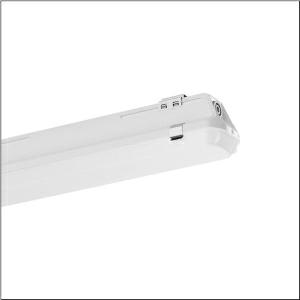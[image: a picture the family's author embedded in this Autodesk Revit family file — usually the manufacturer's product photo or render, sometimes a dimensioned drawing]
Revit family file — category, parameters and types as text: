
# Revit family: monsun_r__11_51fp208p430h_cbd4
name_source: partatom
category: Lighting Fixtures
units: mm (PartAtom-declared; Revit-internal decimal feet)

## family parameters
Cut with Voids When Loaded = No
Host = Face
Light Source = No
Part Type = Normal
Room Calculation Point = No
Round Connector Dimension = Use Diameter
Shared = No

## types (1)
- Monsun® 11 (1 x LED, 3990 lm, 24.8 W, 4000K)
    Apparent Load = 25 VA
    CIE Flux Codes = 45 75 93 94 100
    Color Rendering = 80
    Color Temperature = 4000K
    Default Elevation = 1800 mm
    Description = Monsun® 11, damp-proof luminaire, chain hanger, primary optical cover: enclosure, of PC, light emission: direct distribution, primary light characteristic: symmetric, installation type: suspended mounting, surface-mounted, horizontal mounting, vertical mounting, LED, rated luminous flux: 3.990lm, luminous efficacy: 161lm/W, light colour: 840, colour temperature: 4000K, control gear: ECG, with terminal, 3-pole, max. 2.5mm², mains connection: 220..240V, AC, 50/60Hz, rated input power: 25W, luminaire housing, of glass-fibre reinforced polyester, uncoated, bright grey, incl. chain hanger, length: 1.590mm, width: 90mm, height: 88mm, clip for enclosure, of stainless steel (V2A), ceiling mounting element, of stainless steel (V2A), chain hanger, of stainless steel (V2A), protection rating (complete): IP66, insulation class (complete): insulation class I (protective earthing), certification: CE, ENEC, VDE, UKCA, protection symbol: D, impact resistance: IK08, permissible operating ambient temperature: -35..+40°C, standard: EN 50419, EN 60598-2-1, no direct snow, no direct sun, no direct rain, for indoor or canopied outdoor use, corresponds to IFS (International Featured Standards) requirements for safety and quality in the food industry, contact your sales advisor before using the luminaires in applications with unclear chemical exposure, large temperature fluctuations or condensation-forming humidity, LABS conformity tested according to VDMA 24364:2018-05, packaging unit: 1 piece
    Height = 89 mm
    Lamp = 1 x LED
    Lamp Light Flux = 3990 lm
    Lamp Power = 24.8 W
    Lamp count = 1
    Length = 1590 mm
    Luminous efficacy = 161 lm/W
    Manufacturer = Siteco
    ModVariant = No
    Model = 51FP208P430H
    Mounting Place = Ceiling
    Mounting Type = Surface mounted
    Number of Poles = 1
    OnlyDefault = Yes
    Power Factor = 1
    Product Name = Monsun® 11
    Product group = damp-proof luminaire
    ProductGroupID = 300
    Protection Class = Protection class I
    Protection Degree = IP 66
    RLX_Detail_Level = 1
    RLX_Emergency_Light_Flux = 0 lm
    RLX_Emergency_Type = 0
    RLX_Emergency_Type_DB = No
    RlxData = <blob elided: 88433 chars, md5=e6f157c5>
    Socket = socket
    Standby Power = 0 W
    System Light Flux = 3990 lm
    System Power = 25 W
    Type Comments = Product without accessories
    Type Image = l_1319650.jpg
    URL = http://relux.com
    VarID = ---
    Voltage = 0 V
    Weight = 0.00 kg
    Width = 90 mm

## geometry (parser evidence)
native form markers: Blend x4, Sweep x12
no freeform markers — native parametric forms only
